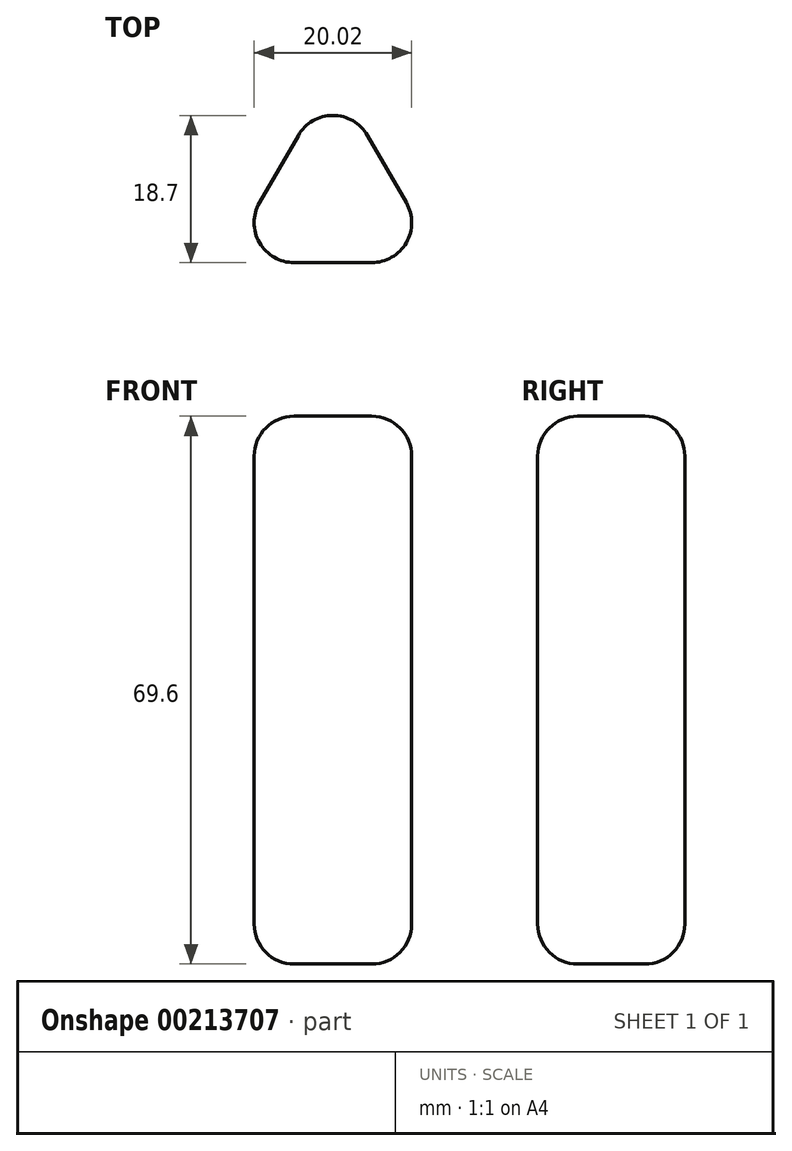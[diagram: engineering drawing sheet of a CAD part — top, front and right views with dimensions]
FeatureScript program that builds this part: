
annotation { "Feature Type Name" : "Feature", "Feature Type Description" : "" }
export const myFeature = defineFeature(function(context is Context, id is Id, definition is map)
    precondition{}
    {
        {
            var Q0;
            Q0=qCreatedBy(makeId("Top.planeOp"),FACE);
            var sketch = newSketch(context, id + "F0", { "sketchPlane" : qUnion([Q0])});
            skCircle(sketch, "E0.cCircle", {"center": v(0, 0) * mm, "radius": 7.93 * mm, "construction": true});
            skLineSegment(sketch, "E0.0", {"start": v(13.73, -7.93) * mm, "end": v(-13.73, -7.93) * mm});
            skLineSegment(sketch, "E0.1", {"start": v(-13.73, -7.93) * mm, "end": v(0, 15.85) * mm});
            skLineSegment(sketch, "E0.2", {"start": v(0, 15.85) * mm, "end": v(13.73, -7.93) * mm});
            skPoint(sketch, "E0.0.midPoint", {"position": v(0, -7.93) * mm});
            skSolve(sketch);
        }
        {
            var Q0;
            Q0 = qSketchRegion(id + "F0", true);
            extrude(context, id + "F1", {"entities" : qUnion([Q0]), "depth" : 69.6 * mm});
        }
        {
            var Q0;
            Q0=makeQuery(id+"F1.opExtrude","SWEPT_EDGE",EDGE,{"disambiguationData":[OSD([sQuery(id+"F0.wireOp",EDGE,"E0.1"),sQuery(id+"F0.wireOp",EDGE,"E0.2")])]});
            var Q1;
            Q1=makeQuery(id+"F1.opExtrude","CAP_EDGE",EDGE,{"disambiguationData":[OSD([sQuery(id+"F0.wireOp",EDGE,"E0.1")])],"isStart":false});
            var Q2;
            Q2=makeQuery(id+"F1.opExtrude","CAP_EDGE",EDGE,{"disambiguationData":[OSD([sQuery(id+"F0.wireOp",EDGE,"E0.2")])],"isStart":false});
            var Q3;
            Q3=makeQuery(id+"F1.opExtrude","SWEPT_EDGE",EDGE,{"disambiguationData":[OSD([sQuery(id+"F0.wireOp",EDGE,"E0.0"),sQuery(id+"F0.wireOp",EDGE,"E0.1")])]});
            var Q4;
            Q4=makeQuery(id+"F1.opExtrude","CAP_EDGE",EDGE,{"disambiguationData":[OSD([sQuery(id+"F0.wireOp",EDGE,"E0.0")])],"isStart":false});
            var Q5;
            Q5=makeQuery(id+"F1.opExtrude","CAP_EDGE",EDGE,{"disambiguationData":[OSD([sQuery(id+"F0.wireOp",EDGE,"E0.1")])],"isStart":true});
            var Q6;
            Q6=makeQuery(id+"F1.opExtrude","SWEPT_EDGE",EDGE,{"disambiguationData":[OSD([sQuery(id+"F0.wireOp",EDGE,"E0.0"),sQuery(id+"F0.wireOp",EDGE,"E0.2")])]});
            var Q7;
            Q7=makeQuery(id+"F1.opExtrude","CAP_EDGE",EDGE,{"disambiguationData":[OSD([sQuery(id+"F0.wireOp",EDGE,"E0.2")])],"isStart":true});
            var Q8;
            Q8=makeQuery(id+"F1.opExtrude","CAP_EDGE",EDGE,{"disambiguationData":[OSD([sQuery(id+"F0.wireOp",EDGE,"E0.0")])],"isStart":true});
            fillet(context, id + "F2", {"entities" : qUnion([Q0, Q1, Q2, Q3, Q4, Q5, Q6, Q7, Q8]), "radius" : 5.08 * mm, "tangentPropagation" : true, "allowEdgeOverflow" : false});
        }
    });
